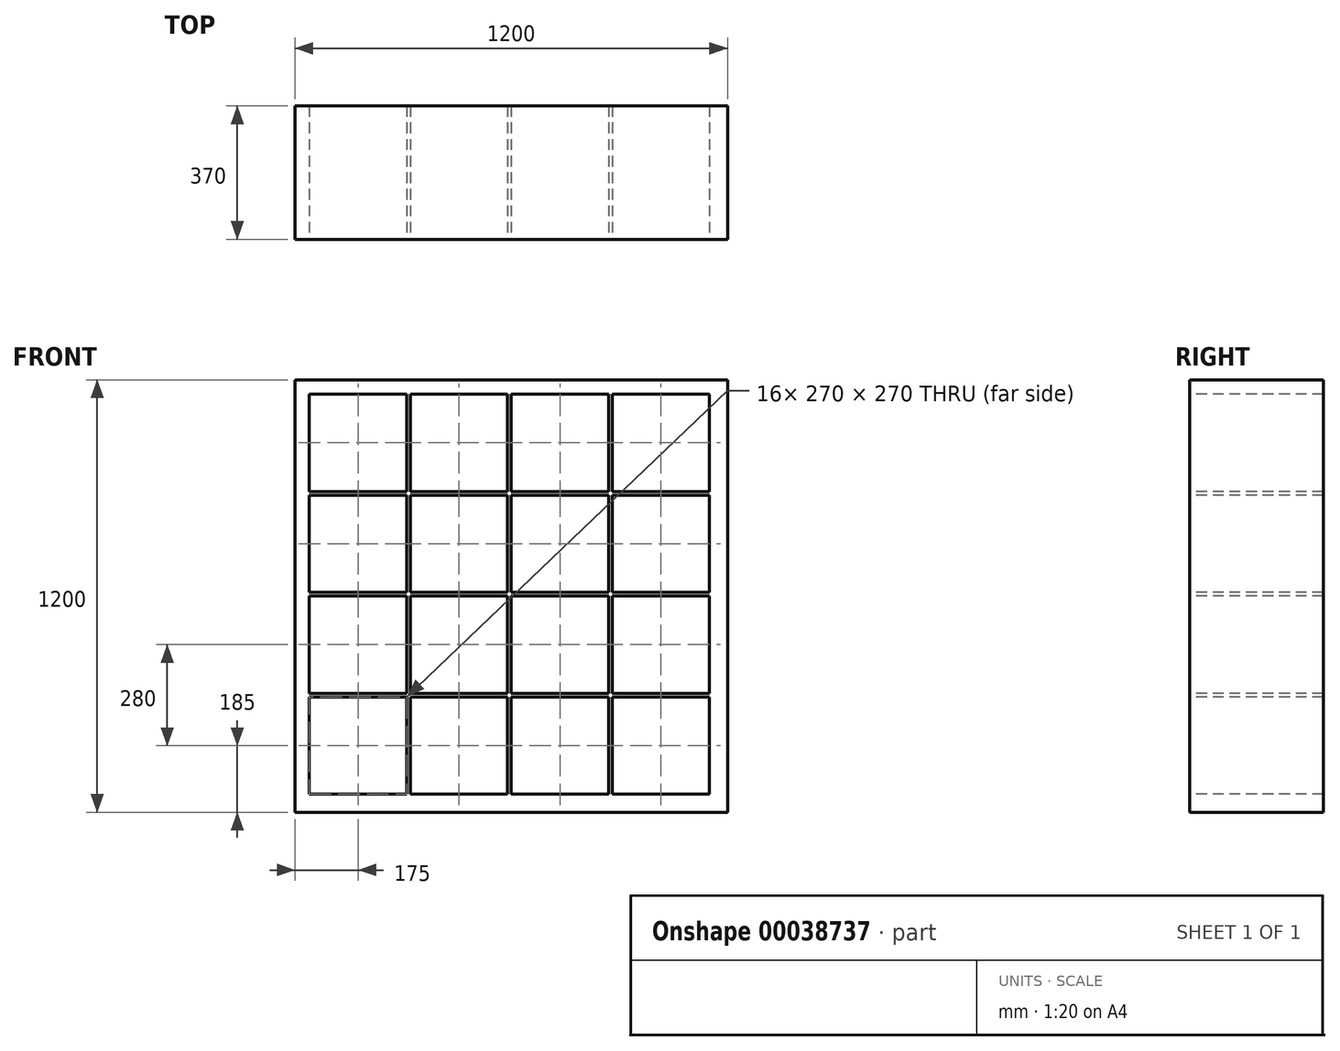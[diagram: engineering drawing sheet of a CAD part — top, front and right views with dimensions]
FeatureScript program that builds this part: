
annotation { "Feature Type Name" : "Feature", "Feature Type Description" : "" }
export const myFeature = defineFeature(function(context is Context, id is Id, definition is map)
    precondition{}
    {
        {
            var Q0;
            Q0=qCreatedBy(makeId("Top.planeOp"),FACE);
            var sketch = newSketch(context, id + "F0", { "sketchPlane" : qUnion([Q0])});
            skLineSegment(sketch, "E0.bottom", {"start": v(-63.05, 308.8) * mm, "end": v(1136.95, 308.8) * mm});
            skLineSegment(sketch, "E0.top", {"start": v(-63.05, -61.2) * mm, "end": v(1136.95, -61.2) * mm});
            skLineSegment(sketch, "E0.left", {"start": v(-63.05, 308.8) * mm, "end": v(-63.05, -61.2) * mm});
            skLineSegment(sketch, "E0.right", {"start": v(1136.95, 308.8) * mm, "end": v(1136.95, -61.2) * mm});
            skSolve(sketch);
        }
        {
            var Q0;
            Q0=makeQuery(id+"F0.imprint","IMPRINT",FACE,{"disambiguationData":[TD([[makeQuery(id+"F0.imprint","IMPRINT",EDGE,{"derivedFrom":sQuery(id+"F0.wireOp",EDGE,"E0.bottom")}),-1.0]])]});
            extrude(context, id + "F1", {"entities" : qUnion([Q0]), "depth" : 1200 * mm});
        }
        {
            var Q0;
            Q0=makeQuery(id+"F1.opExtrude","SWEPT_FACE",FACE,{"disambiguationData":[OSD([sQuery(id+"F0.wireOp",EDGE,"E0.top")])]});
            var sketch = newSketch(context, id + "F2", { "sketchPlane" : qUnion([Q0])});
            skLineSegment(sketch, "E1.bottom", {"start": v(-23.05, 1160) * mm, "end": v(246.95, 1160) * mm});
            skLineSegment(sketch, "E1.top", {"start": v(-23.05, 890) * mm, "end": v(246.95, 890) * mm});
            skLineSegment(sketch, "E1.left", {"start": v(-23.05, 1160) * mm, "end": v(-23.05, 890) * mm});
            skLineSegment(sketch, "E1.right", {"start": v(246.95, 1160) * mm, "end": v(246.95, 890) * mm});
            skLineSegment(sketch, "E2.0.1.0", {"start": v(246.95, 880) * mm, "end": v(246.95, 610) * mm});
            skLineSegment(sketch, "E2.0.1.1", {"start": v(-23.05, 880) * mm, "end": v(-23.05, 610) * mm});
            skLineSegment(sketch, "E2.0.1.2", {"start": v(-23.05, 610) * mm, "end": v(246.95, 610) * mm});
            skLineSegment(sketch, "E2.0.1.3", {"start": v(-23.05, 880) * mm, "end": v(246.95, 880) * mm});
            skLineSegment(sketch, "E2.0.2.0", {"start": v(246.95, 600) * mm, "end": v(246.95, 330) * mm});
            skLineSegment(sketch, "E2.0.2.1", {"start": v(-23.05, 600) * mm, "end": v(-23.05, 330) * mm});
            skLineSegment(sketch, "E2.0.2.2", {"start": v(-23.05, 330) * mm, "end": v(246.95, 330) * mm});
            skLineSegment(sketch, "E2.0.2.3", {"start": v(-23.05, 600) * mm, "end": v(246.95, 600) * mm});
            skLineSegment(sketch, "E2.0.3.0", {"start": v(246.95, 320) * mm, "end": v(246.95, 50) * mm});
            skLineSegment(sketch, "E2.0.3.1", {"start": v(-23.05, 320) * mm, "end": v(-23.05, 50) * mm});
            skLineSegment(sketch, "E2.0.3.2", {"start": v(-23.05, 50) * mm, "end": v(246.95, 50) * mm});
            skLineSegment(sketch, "E2.0.3.3", {"start": v(-23.05, 320) * mm, "end": v(246.95, 320) * mm});
            skLineSegment(sketch, "E2.1.0.0", {"start": v(526.95, 1160) * mm, "end": v(526.95, 890) * mm});
            skLineSegment(sketch, "E2.1.0.1", {"start": v(256.95, 1160) * mm, "end": v(256.95, 890) * mm});
            skLineSegment(sketch, "E2.1.0.2", {"start": v(256.95, 890) * mm, "end": v(526.95, 890) * mm});
            skLineSegment(sketch, "E2.1.0.3", {"start": v(256.95, 1160) * mm, "end": v(526.95, 1160) * mm});
            skLineSegment(sketch, "E2.1.1.0", {"start": v(526.95, 880) * mm, "end": v(526.95, 610) * mm});
            skLineSegment(sketch, "E2.1.1.1", {"start": v(256.95, 880) * mm, "end": v(256.95, 610) * mm});
            skLineSegment(sketch, "E2.1.1.2", {"start": v(256.95, 610) * mm, "end": v(526.95, 610) * mm});
            skLineSegment(sketch, "E2.1.1.3", {"start": v(256.95, 880) * mm, "end": v(526.95, 880) * mm});
            skLineSegment(sketch, "E2.1.2.0", {"start": v(526.95, 600) * mm, "end": v(526.95, 330) * mm});
            skLineSegment(sketch, "E2.1.2.1", {"start": v(256.95, 600) * mm, "end": v(256.95, 330) * mm});
            skLineSegment(sketch, "E2.1.2.2", {"start": v(256.95, 330) * mm, "end": v(526.95, 330) * mm});
            skLineSegment(sketch, "E2.1.2.3", {"start": v(256.95, 600) * mm, "end": v(526.95, 600) * mm});
            skLineSegment(sketch, "E2.1.3.0", {"start": v(526.95, 320) * mm, "end": v(526.95, 50) * mm});
            skLineSegment(sketch, "E2.1.3.1", {"start": v(256.95, 320) * mm, "end": v(256.95, 50) * mm});
            skLineSegment(sketch, "E2.1.3.2", {"start": v(256.95, 50) * mm, "end": v(526.95, 50) * mm});
            skLineSegment(sketch, "E2.1.3.3", {"start": v(256.95, 320) * mm, "end": v(526.95, 320) * mm});
            skLineSegment(sketch, "E2.2.0.0", {"start": v(806.95, 1160) * mm, "end": v(806.95, 890) * mm});
            skLineSegment(sketch, "E2.2.0.1", {"start": v(536.95, 1160) * mm, "end": v(536.95, 890) * mm});
            skLineSegment(sketch, "E2.2.0.2", {"start": v(536.95, 890) * mm, "end": v(806.95, 890) * mm});
            skLineSegment(sketch, "E2.2.0.3", {"start": v(536.95, 1160) * mm, "end": v(806.95, 1160) * mm});
            skLineSegment(sketch, "E2.2.1.0", {"start": v(806.95, 880) * mm, "end": v(806.95, 610) * mm});
            skLineSegment(sketch, "E2.2.1.1", {"start": v(536.95, 880) * mm, "end": v(536.95, 610) * mm});
            skLineSegment(sketch, "E2.2.1.2", {"start": v(536.95, 610) * mm, "end": v(806.95, 610) * mm});
            skLineSegment(sketch, "E2.2.1.3", {"start": v(536.95, 880) * mm, "end": v(806.95, 880) * mm});
            skLineSegment(sketch, "E2.2.2.0", {"start": v(806.95, 600) * mm, "end": v(806.95, 330) * mm});
            skLineSegment(sketch, "E2.2.2.1", {"start": v(536.95, 600) * mm, "end": v(536.95, 330) * mm});
            skLineSegment(sketch, "E2.2.2.2", {"start": v(536.95, 330) * mm, "end": v(806.95, 330) * mm});
            skLineSegment(sketch, "E2.2.2.3", {"start": v(536.95, 600) * mm, "end": v(806.95, 600) * mm});
            skLineSegment(sketch, "E2.2.3.0", {"start": v(806.95, 320) * mm, "end": v(806.95, 50) * mm});
            skLineSegment(sketch, "E2.2.3.1", {"start": v(536.95, 320) * mm, "end": v(536.95, 50) * mm});
            skLineSegment(sketch, "E2.2.3.2", {"start": v(536.95, 50) * mm, "end": v(806.95, 50) * mm});
            skLineSegment(sketch, "E2.2.3.3", {"start": v(536.95, 320) * mm, "end": v(806.95, 320) * mm});
            skLineSegment(sketch, "E2.3.0.0", {"start": v(1086.95, 1160) * mm, "end": v(1086.95, 890) * mm});
            skLineSegment(sketch, "E2.3.0.1", {"start": v(816.95, 1160) * mm, "end": v(816.95, 890) * mm});
            skLineSegment(sketch, "E2.3.0.2", {"start": v(816.95, 890) * mm, "end": v(1086.95, 890) * mm});
            skLineSegment(sketch, "E2.3.0.3", {"start": v(816.95, 1160) * mm, "end": v(1086.95, 1160) * mm});
            skLineSegment(sketch, "E2.3.1.0", {"start": v(1086.95, 880) * mm, "end": v(1086.95, 610) * mm});
            skLineSegment(sketch, "E2.3.1.1", {"start": v(816.95, 880) * mm, "end": v(816.95, 610) * mm});
            skLineSegment(sketch, "E2.3.1.2", {"start": v(816.95, 610) * mm, "end": v(1086.95, 610) * mm});
            skLineSegment(sketch, "E2.3.1.3", {"start": v(816.95, 880) * mm, "end": v(1086.95, 880) * mm});
            skLineSegment(sketch, "E2.3.2.0", {"start": v(1086.95, 600) * mm, "end": v(1086.95, 330) * mm});
            skLineSegment(sketch, "E2.3.2.1", {"start": v(816.95, 600) * mm, "end": v(816.95, 330) * mm});
            skLineSegment(sketch, "E2.3.2.2", {"start": v(816.95, 330) * mm, "end": v(1086.95, 330) * mm});
            skLineSegment(sketch, "E2.3.2.3", {"start": v(816.95, 600) * mm, "end": v(1086.95, 600) * mm});
            skLineSegment(sketch, "E2.3.3.0", {"start": v(1086.95, 320) * mm, "end": v(1086.95, 50) * mm});
            skLineSegment(sketch, "E2.3.3.1", {"start": v(816.95, 320) * mm, "end": v(816.95, 50) * mm});
            skLineSegment(sketch, "E2.3.3.2", {"start": v(816.95, 50) * mm, "end": v(1086.95, 50) * mm});
            skLineSegment(sketch, "E2.3.3.3", {"start": v(816.95, 320) * mm, "end": v(1086.95, 320) * mm});
            skLineSegment(sketch, "E2.direction1", {"start": v(246.95, 890) * mm, "end": v(526.95, 890) * mm, "construction": true});
            skLineSegment(sketch, "E2.direction2", {"start": v(246.95, 890) * mm, "end": v(246.95, 610) * mm, "construction": true});
            skSolve(sketch);
        }
        {
            var Q0;
            Q0=makeQuery(id+"F2.imprint","IMPRINT",FACE,{"disambiguationData":[TD([[makeQuery(id+"F2.imprint","IMPRINT",EDGE,{"derivedFrom":sQuery(id+"F2.wireOp",EDGE,"E1.bottom")}),-1.0]])]});
            var Q1;
            Q1=makeQuery(id+"F2.imprint","IMPRINT",FACE,{"disambiguationData":[TD([[makeQuery(id+"F2.imprint","IMPRINT",EDGE,{"derivedFrom":sQuery(id+"F2.wireOp",EDGE,"E2.1.0.0")}),-1.0]])]});
            var Q2;
            Q2=makeQuery(id+"F2.imprint","IMPRINT",FACE,{"disambiguationData":[TD([[makeQuery(id+"F2.imprint","IMPRINT",EDGE,{"derivedFrom":sQuery(id+"F2.wireOp",EDGE,"E2.2.0.0")}),-1.0]])]});
            var Q3;
            Q3=makeQuery(id+"F2.imprint","IMPRINT",FACE,{"disambiguationData":[TD([[makeQuery(id+"F2.imprint","IMPRINT",EDGE,{"derivedFrom":sQuery(id+"F2.wireOp",EDGE,"E2.3.0.0")}),-1.0]])]});
            var Q4;
            Q4=makeQuery(id+"F2.imprint","IMPRINT",FACE,{"disambiguationData":[TD([[makeQuery(id+"F2.imprint","IMPRINT",EDGE,{"derivedFrom":sQuery(id+"F2.wireOp",EDGE,"E2.3.1.0")}),-1.0]])]});
            var Q5;
            Q5=makeQuery(id+"F2.imprint","IMPRINT",FACE,{"disambiguationData":[TD([[makeQuery(id+"F2.imprint","IMPRINT",EDGE,{"derivedFrom":sQuery(id+"F2.wireOp",EDGE,"E2.2.1.0")}),-1.0]])]});
            var Q6;
            Q6=makeQuery(id+"F2.imprint","IMPRINT",FACE,{"disambiguationData":[TD([[makeQuery(id+"F2.imprint","IMPRINT",EDGE,{"derivedFrom":sQuery(id+"F2.wireOp",EDGE,"E2.1.1.0")}),-1.0]])]});
            var Q7;
            Q7=makeQuery(id+"F2.imprint","IMPRINT",FACE,{"disambiguationData":[TD([[makeQuery(id+"F2.imprint","IMPRINT",EDGE,{"derivedFrom":sQuery(id+"F2.wireOp",EDGE,"E2.0.1.0")}),-1.0]])]});
            var Q8;
            Q8=makeQuery(id+"F2.imprint","IMPRINT",FACE,{"disambiguationData":[TD([[makeQuery(id+"F2.imprint","IMPRINT",EDGE,{"derivedFrom":sQuery(id+"F2.wireOp",EDGE,"E2.0.2.0")}),-1.0]])]});
            var Q9;
            Q9=makeQuery(id+"F2.imprint","IMPRINT",FACE,{"disambiguationData":[TD([[makeQuery(id+"F2.imprint","IMPRINT",EDGE,{"derivedFrom":sQuery(id+"F2.wireOp",EDGE,"E2.1.2.0")}),-1.0]])]});
            var Q10;
            Q10=makeQuery(id+"F2.imprint","IMPRINT",FACE,{"disambiguationData":[TD([[makeQuery(id+"F2.imprint","IMPRINT",EDGE,{"derivedFrom":sQuery(id+"F2.wireOp",EDGE,"E2.2.2.0")}),-1.0]])]});
            var Q11;
            Q11=makeQuery(id+"F2.imprint","IMPRINT",FACE,{"disambiguationData":[TD([[makeQuery(id+"F2.imprint","IMPRINT",EDGE,{"derivedFrom":sQuery(id+"F2.wireOp",EDGE,"E2.3.2.0")}),-1.0]])]});
            var Q12;
            Q12=makeQuery(id+"F2.imprint","IMPRINT",FACE,{"disambiguationData":[TD([[makeQuery(id+"F2.imprint","IMPRINT",EDGE,{"derivedFrom":sQuery(id+"F2.wireOp",EDGE,"E2.3.3.0")}),-1.0]])]});
            var Q13;
            Q13=makeQuery(id+"F2.imprint","IMPRINT",FACE,{"disambiguationData":[TD([[makeQuery(id+"F2.imprint","IMPRINT",EDGE,{"derivedFrom":sQuery(id+"F2.wireOp",EDGE,"E2.2.3.0")}),-1.0]])]});
            var Q14;
            Q14=makeQuery(id+"F2.imprint","IMPRINT",FACE,{"disambiguationData":[TD([[makeQuery(id+"F2.imprint","IMPRINT",EDGE,{"derivedFrom":sQuery(id+"F2.wireOp",EDGE,"E2.1.3.0")}),-1.0]])]});
            var Q15;
            Q15=makeQuery(id+"F2.imprint","IMPRINT",FACE,{"disambiguationData":[TD([[makeQuery(id+"F2.imprint","IMPRINT",EDGE,{"derivedFrom":sQuery(id+"F2.wireOp",EDGE,"E2.0.3.0")}),-1.0]])]});
            extrude(context, id + "F3", {"entities" : qUnion([Q0, Q1, Q2, Q3, Q4, Q5, Q6, Q7, Q8, Q9, Q10, Q11, Q12, Q13, Q14, Q15]), "operationType" : NewBodyOperationType.REMOVE, "endBound" : BoundingType.THROUGH_ALL, "oppositeDirection" : true, "depth" : 25 * mm});
        }
    });
